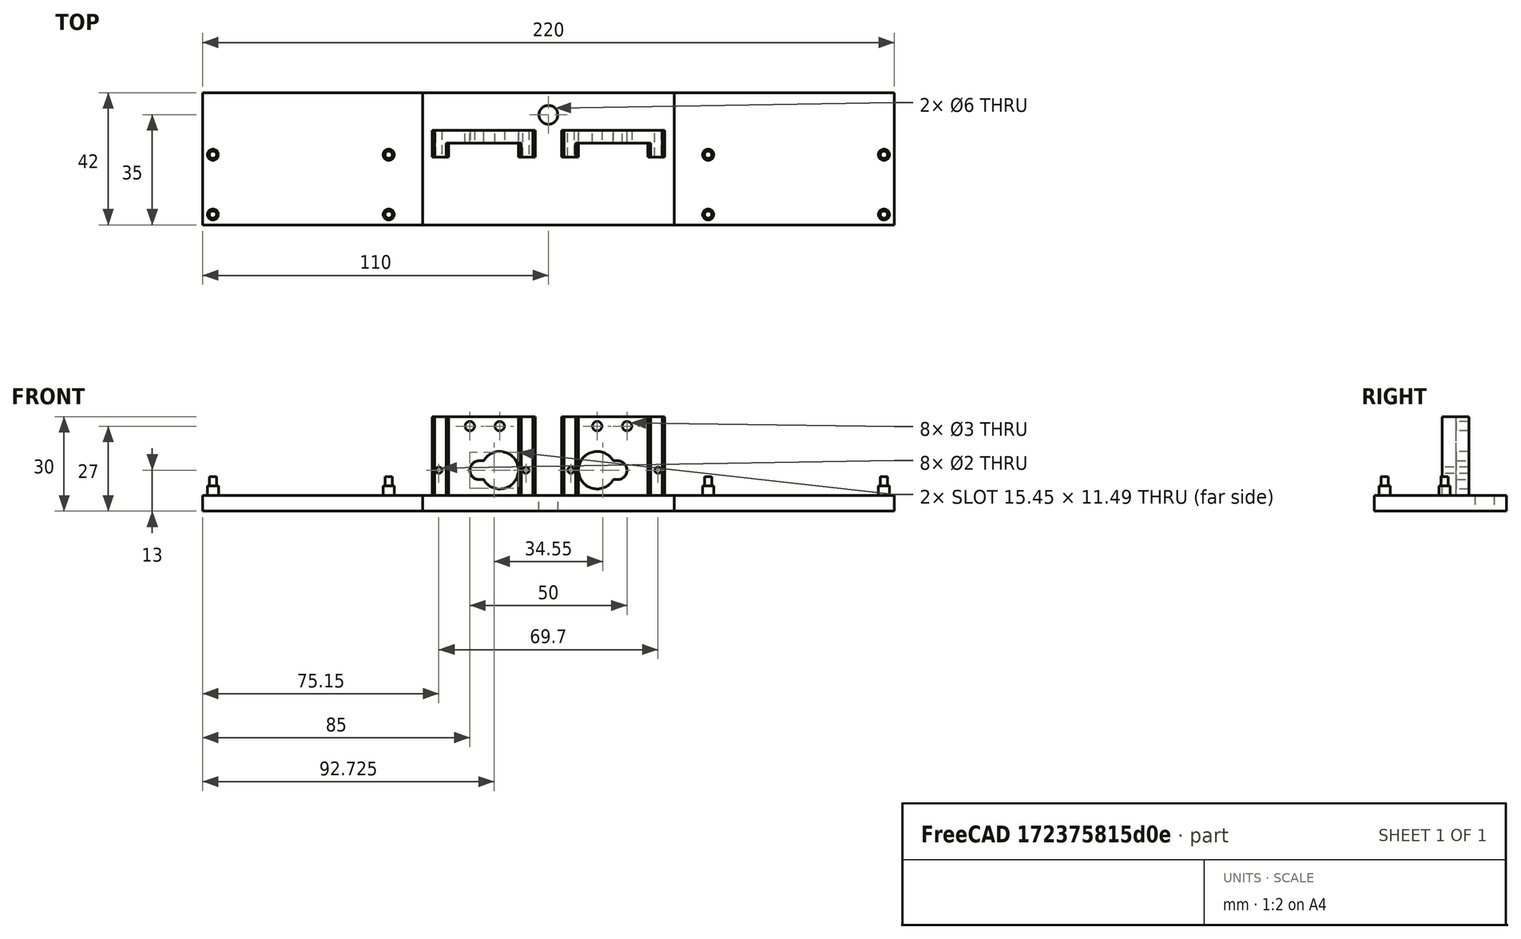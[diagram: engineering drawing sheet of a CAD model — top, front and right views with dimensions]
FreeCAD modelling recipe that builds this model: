
FCSTD DOCUMENT  (FreeCAD 1.0R39319 (Git))
Label: TrainOrderServoInLine
License: All rights reserved
objects: Sketcher::SketchObject×6, PartDesign::Pad×4, Mesh::Feature×4, PartDesign::Pocket×2, PartDesign::Body×1, App::Part×1, Part::Feature×1
note: 32 computed .brp shape members not serialized (recipe doc carries the construction recipe); baked Part::Feature solids carry a one-line shape summary decoded from their .brp

FEATURE [Sketcher::SketchObject] Sketch
  ArcFitTolerance = 1e-06
  AttachmentSupport = -> [XY_Plane001]
  FullyConstrained = true
  MakeInternals = false
  MapMode = 5
  sketch-geometry (5):
    g0: LineSegment StartX=110 StartY=7 StartZ=0 EndX=-40 EndY=7 EndZ=0
    g1: Circle CenterX=0 CenterY=0 CenterZ=0 NormalX=0 NormalY=0 NormalZ=1 AngleXU=0 Radius=3
    g2: LineSegment StartX=110 StartY=-35 StartZ=0 EndX=110 EndY=7 EndZ=0
    g3: LineSegment StartX=-40 StartY=7 StartZ=0 EndX=-40 EndY=-35 EndZ=0
    g4: LineSegment StartX=-40 StartY=-35 StartZ=0 EndX=110 EndY=-35 EndZ=0
  constraints (16):
    c: Distance(g3,g0) = 42
    c: Diameter(g1) = 6
    c: Vertical(g2)
    c: DistanceX(g0,g0) = 150
    c: DistanceY(g4,g-1) = 35
    c: Horizontal(g0)
    c: Coincident(g0,g2)
    c: Coincident(g3,g0)
    c: Vertical(g3)
    c: Coincident(g4,g2)
    c: Horizontal(g4)
    c: Distance(g3,g-2) = 40
    c: Equal(g3,g2)
    c: Equal(g0,g4)
    c: Distance(g1,g0) = 7
    c: Distance(g1,g3) = 40
FEATURE [PartDesign::Pad] Pad
  Direction = (0,0,1)
  Length = 5
  Length2 = 10
  Profile = -> Sketch
  ReferenceAxis = -> Sketch [N_Axis]
  Suppressed = false
  Type = 0
FEATURE [Sketcher::SketchObject] Sketch001
  ArcFitTolerance = 1e-06
  AttachmentSupport = -> [Pad]
  ExternalGeometry = -> [Pad]
  FullyConstrained = true
  MakeInternals = false
  MapMode = 5
  Placement = pos=(0,0,5) rot=(0,0,1;0rad)
  sketch-geometry (16):
    g0: LineSegment StartX=-5 StartY=-5 StartZ=0 EndX=-37 EndY=-5 EndZ=0
    g1: LineSegment StartX=-37 StartY=-5 StartZ=0 EndX=-37 EndY=-13.4 EndZ=0
    g2: LineSegment StartX=-37 StartY=-13.4 StartZ=0 EndX=-32.5 EndY=-13.4 EndZ=0
    g3: LineSegment StartX=-32.5 StartY=-13.4 StartZ=0 EndX=-32.5 EndY=-9 EndZ=0
    g4: LineSegment StartX=-32.5 StartY=-9 StartZ=0 EndX=-9.5 EndY=-9 EndZ=0
    g5: LineSegment StartX=-9.5 StartY=-9 StartZ=0 EndX=-9.5 EndY=-13.4 EndZ=0
    g6: LineSegment StartX=-9.5 StartY=-13.4 StartZ=0 EndX=-5 EndY=-13.4 EndZ=0
    g7: LineSegment StartX=-5 StartY=-13.4 StartZ=0 EndX=-5 EndY=-5 EndZ=0
    g8: LineSegment StartX=4.18082 StartY=-5 StartZ=0 EndX=36.1808 EndY=-5 EndZ=0
    g9: LineSegment StartX=36.1808 StartY=-5 StartZ=0 EndX=36.1808 EndY=-13.4 EndZ=0
    g10: LineSegment StartX=36.1808 StartY=-13.4 StartZ=0 EndX=31.6808 EndY=-13.4 EndZ=0
    g11: LineSegment StartX=31.6808 StartY=-13.4 StartZ=0 EndX=31.6808 EndY=-9 EndZ=0
    g12: LineSegment StartX=31.6808 StartY=-9 StartZ=0 EndX=8.68082 EndY=-9 EndZ=0
    g13: LineSegment StartX=8.68082 StartY=-9 StartZ=0 EndX=8.68082 EndY=-13.4 EndZ=0
    g14: LineSegment StartX=8.68082 StartY=-13.4 StartZ=0 EndX=4.18082 EndY=-13.4 EndZ=0
    g15: LineSegment StartX=4.18082 StartY=-13.4 StartZ=0 EndX=4.18082 EndY=-5 EndZ=0
  constraints (48):
    c: Horizontal(g0)
    c: Vertical(g1)
    c: Coincident(g1,g2)
    c: Horizontal(g2)
    c: Coincident(g2,g3)
    c: Vertical(g3)
    c: Coincident(g3,g4)
    c: Horizontal(g4)
    c: Coincident(g4,g5)
    c: Vertical(g5)
    c: Coincident(g5,g6)
    c: Horizontal(g6)
    c: Coincident(g6,g7)
    c: Coincident(g7,g0)
    c: Vertical(g7)
    c: DistanceY(g0,g-1) = 5
    c: DistanceX(g0,g-1) = 5
    c: Coincident(g1,g0)
    c: Distance(g6,g6) = 4.5
    c: DistanceX(g4,g4) = 23
    c: DistanceY(g7,g7) = 8.4
    c: DistanceY(g3,g3) = 4.4
    c: Horizontal(g8)
    c: Vertical(g9)
    c: Coincident(g9,g10)
    c: Horizontal(g10)
    c: Coincident(g10,g11)
    c: Vertical(g11)
    c: Coincident(g11,g12)
    c: Horizontal(g12)
    c: Coincident(g12,g13)
    c: Vertical(g13)
    c: Coincident(g13,g14)
    c: Horizontal(g14)
    c: Coincident(g14,g15)
    c: Coincident(g15,g8)
    c: Vertical(g15)
    c: DistanceX(g0,g0) = 32
    c: Horizontal(g0,g8)
    c: Horizontal(g4,g12)
    c: Horizontal(g2,g5)
    c: Horizontal(g6,g14)
    c: Horizontal(g13,g10)
    c: Coincident(g8,g9)
    c: Equal(g10,g14)
    c: Equal(g14,g6)
    c: Equal(g4,g12)
    c: Equal(g8,g0)
FEATURE [PartDesign::Pad] Pad001
  BaseFeature = -> Pad
  Direction = (0,0,1)
  Length = 25
  Length2 = 10
  Profile = -> Sketch001
  ReferenceAxis = -> Sketch001 [N_Axis]
  Suppressed = false
  Type = 0
FEATURE [Sketcher::SketchObject] Sketch002
  ArcFitTolerance = 1e-06
  AttachmentSupport = -> [Pad001]
  ExternalGeometry = -> [Pad001]
  FullyConstrained = true
  MakeInternals = false
  MapMode = 5
  Placement = pos=(0,-9,0) rot=(1,0,0;1.5708rad)
  sketch-geometry (8):
    g0: ArcOfCircle CenterX=-15.45 CenterY=13 CenterZ=0 NormalX=0 NormalY=0 NormalZ=1 AngleXU=0 Radius=5.95 StartAngle=3.67005 EndAngle=8.89632
    g1: Circle CenterX=-7.15 CenterY=13 CenterZ=0 NormalX=0 NormalY=0 NormalZ=1 AngleXU=0 Radius=1
    g2: Circle CenterX=-34.85 CenterY=13 CenterZ=0 NormalX=0 NormalY=0 NormalZ=1 AngleXU=0 Radius=1
    g3: ArcOfCircle CenterX=-21.95 CenterY=13 CenterZ=0 NormalX=0 NormalY=0 NormalZ=1 AngleXU=0 Radius=3 StartAngle=1.5708 EndAngle=4.71239
    g4: LineSegment StartX=-21.95 StartY=10 StartZ=0 EndX=-20.5883 EndY=10 EndZ=0
    g5: LineSegment StartX=-21.95 StartY=16 StartZ=0 EndX=-20.5883 EndY=16 EndZ=0
    g6: Circle CenterX=-25 CenterY=27 CenterZ=0 NormalX=0 NormalY=0 NormalZ=1 AngleXU=0 Radius=1.5
    g7: Circle CenterX=-15.5 CenterY=27 CenterZ=0 NormalX=0 NormalY=0 NormalZ=1 AngleXU=0 Radius=1.5
  constraints (24):
    c: Diameter(g0) = 11.9
    c: DistanceY(g-4,g0) = 8
    c: Tangent(g0,g-4)
    c: Diameter(g1) = 2
    c: Diameter(g2) = 2
    c: Horizontal(g1,g0)
    c: Horizontal(g0,g2)
    c: DistanceX(g2,g-5) = 2.35
    c: DistanceX(g-5,g1) = 2.35
    c: Diameter(g3) = 6
    c: Horizontal(g3,g0)
    c: DistanceX(g3,g0) = 6.5
    c: Horizontal(g4)
    c: Horizontal(g5)
    c: Diameter(g6) = 3
    c: Diameter(g7) = 3
    c: Horizontal(g6,g7)
    c: DistanceX(g6,g7) = 9.5
    c: DistanceX(g7,g-4) = 6
    c: Tangent(g3,g5) = 1.5708
    c: Tangent(g3,g4) = -1.5708
    c: Coincident(g0,g4)
    c: Coincident(g0,g5)
    c: DistanceY(g0,g7) = 14
FEATURE [PartDesign::Pocket] Pocket
  BaseFeature = -> Pad001
  Direction = (0,1,-2e-16)
  Length = 5
  Length2 = 5
  Midplane = true
  Profile = -> Sketch002
  ReferenceAxis = -> Sketch002 [N_Axis]
  Suppressed = false
  Type = 1
FEATURE [Sketcher::SketchObject] Sketch003
  ArcFitTolerance = 1e-06
  AttachmentSupport = -> [Pocket]
  ExternalGeometry = -> [Pocket]
  FullyConstrained = true
  MakeInternals = false
  MapMode = 5
  Placement = pos=(0,-5,0) rot=(0,0.707107,0.707107;3.14159rad)
  sketch-geometry (8):
    g0: ArcOfCircle CenterX=-22 CenterY=13 CenterZ=0 NormalX=0 NormalY=0 NormalZ=1 AngleXU=0 Radius=3 StartAngle=1.5708 EndAngle=4.71239
    g1: Circle CenterX=-25 CenterY=27 CenterZ=0 NormalX=0 NormalY=0 NormalZ=1 AngleXU=0 Radius=1.5
    g2: Circle CenterX=-15.5 CenterY=27 CenterZ=0 NormalX=0 NormalY=0 NormalZ=1 AngleXU=0 Radius=1.5
    g3: Circle CenterX=-7.15 CenterY=13 CenterZ=0 NormalX=0 NormalY=0 NormalZ=1 AngleXU=0 Radius=1
    g4: Circle CenterX=-34.85 CenterY=13 CenterZ=0 NormalX=0 NormalY=0 NormalZ=1 AngleXU=0 Radius=1
    g5: LineSegment StartX=-22 StartY=16 StartZ=0 EndX=-20.6383 EndY=16 EndZ=0
    g6: LineSegment StartX=-22 StartY=10 StartZ=0 EndX=-20.6383 EndY=10 EndZ=0
    g7: ArcOfCircle CenterX=-15.5 CenterY=13 CenterZ=0 NormalX=0 NormalY=0 NormalZ=1 AngleXU=0 Radius=5.95 StartAngle=3.67005 EndAngle=8.89632
  constraints (25):
    c: Diameter(g0) = 6
    c: Diameter(g1) = 3
    c: Diameter(g2) = 3
    c: Diameter(g3) = 2
    c: Diameter(g4) = 2
    c: Horizontal(g1,g2)
    c: Horizontal(g3,g4)
    c: DistanceX(g1,g2) = 9.5
    c: Horizontal(g5)
    c: Horizontal(g6)
    c: Diameter(g7) = 11.9
    c: DistanceX(g0,g7) = 6.5
    c: Horizontal(g4,g0)
    c: Horizontal(g0,g7)
    c: Vertical(g7,g2)
    c: DistanceY(g7,g2) = 14
    c: Tangent(g0,g5) = 1.5708
    c: Coincident(g7,g5)
    c: Coincident(g7,g6)
    c: DistanceY(g-4,g7) = 8
    c: DistanceX(g7,g-3) = 6
    c: DistanceX(g-3,g3) = 2.35
    c: DistanceX(g4,g-5) = 2.35
    c: Equal(g6,g5)
    c: Coincident(g6,g0)
FEATURE [PartDesign::Pocket] Pocket001
  BaseFeature = -> Pocket
  Direction = (0,-1,2e-16)
  Length = 5
  Length2 = 5
  Midplane = true
  Profile = -> Sketch003
  ReferenceAxis = -> Sketch003 [N_Axis]
  Suppressed = false
  Type = 1
FEATURE [Mesh::Feature] Mesh  label="Pocket001 (Meshed)"
FEATURE [Sketcher::SketchObject] Sketch004
  ArcFitTolerance = 1e-06
  AttachmentSupport = -> [Pocket001]
  ExternalGeometry = -> [Pocket001]
  FullyConstrained = true
  MakeInternals = false
  MapMode = 5
  Placement = pos=(0,0,5) rot=(0,0,1;0rad)
  sketch-geometry (4):
    g0: Circle CenterX=106.7 CenterY=-31.7 CenterZ=0 NormalX=0 NormalY=0 NormalZ=1 AngleXU=0 Radius=1.75
    g1: Circle CenterX=106.7 CenterY=-12.7 CenterZ=0 NormalX=0 NormalY=0 NormalZ=1 AngleXU=0 Radius=1.75
    g2: Circle CenterX=50.8 CenterY=-12.7 CenterZ=0 NormalX=0 NormalY=0 NormalZ=1 AngleXU=0 Radius=1.75
    g3: Circle CenterX=50.8 CenterY=-31.7 CenterZ=0 NormalX=0 NormalY=0 NormalZ=1 AngleXU=0 Radius=1.75
  constraints (12):
    c: Diameter(g0) = 3.5
    c: Diameter(g1) = 3.5
    c: Diameter(g2) = 3.5
    c: Diameter(g3) = 3.5
    c: DistanceY(g-4,g0) = 3.3
    c: DistanceX(g0,g-4) = 3.3
    c: Horizontal(g3,g0)
    c: Horizontal(g2,g1)
    c: Vertical(g2,g3)
    c: Vertical(g1,g0)
    c: DistanceY(g0,g1) = 19
    c: DistanceX(g3,g0) = 55.9
FEATURE [PartDesign::Pad] Pad002
  BaseFeature = -> Pocket001
  Direction = (0,0,1)
  Length = 3
  Length2 = 10
  Profile = -> Sketch004
  ReferenceAxis = -> Sketch004 [N_Axis]
  Suppressed = false
  Type = 0
FEATURE [Mesh::Feature] Mesh001  label="Pad002 (Meshed)"
FEATURE [Sketcher::SketchObject] Sketch005
  ArcFitTolerance = 1e-06
  AttachmentSupport = -> [Pad002]
  ExternalGeometry = -> [Pad002]
  FullyConstrained = true
  MakeInternals = false
  MapMode = 5
  Placement = pos=(0,0,8) rot=(0,0,1;0rad)
  sketch-geometry (4):
    g0: Circle CenterX=50.8 CenterY=-12.7 CenterZ=0 NormalX=0 NormalY=0 NormalZ=1 AngleXU=0 Radius=1.15
    g1: Circle CenterX=50.8 CenterY=-31.7 CenterZ=0 NormalX=0 NormalY=0 NormalZ=1 AngleXU=0 Radius=1.15
    g2: Circle CenterX=106.7 CenterY=-31.7 CenterZ=0 NormalX=0 NormalY=0 NormalZ=1 AngleXU=0 Radius=1.15
    g3: Circle CenterX=106.7 CenterY=-12.7 CenterZ=0 NormalX=0 NormalY=0 NormalZ=1 AngleXU=0 Radius=1.15
  constraints (8):
    c: Diameter(g0) = 2.3
    c: Coincident(g0,g-3)
    c: Diameter(g1) = 2.3
    c: Coincident(g1,g-4)
    c: Diameter(g2) = 2.3
    c: Coincident(g2,g-5)
    c: Diameter(g3) = 2.3
    c: Coincident(g3,g-6)
FEATURE [PartDesign::Pad] Pad003
  BaseFeature = -> Pad002
  Direction = (0,0,1)
  Length = 3
  Length2 = 10
  Profile = -> Sketch005
  ReferenceAxis = -> Sketch005 [N_Axis]
  Suppressed = false
  Type = 0
FEATURE [PartDesign::Body] Body
  AllowCompound = false
  Group = -> [Sketch,Pad,Sketch001,Pad001,Sketch002,Pocket,Sketch003,Pocket001,Sketch004,Pad002,Sketch005,Pad003]
  Origin = -> Origin001
  Tip = -> Pad003
FEATURE [App::Part] Part  label="ServoBase"
  Group = -> [Body]
  Origin = -> Origin
FEATURE [Mesh::Feature] Mesh002  label="Pad003 (Meshed)"
FEATURE [Mesh::Feature] Mesh003  label="ServoBase (Meshed)"
FEATURE [Part::Feature] Body_Flipped  label="TrainOrderServoInLine Flipped"
  shape: bbox 150 x 42 x 30 mm, 58 faces (baked)
